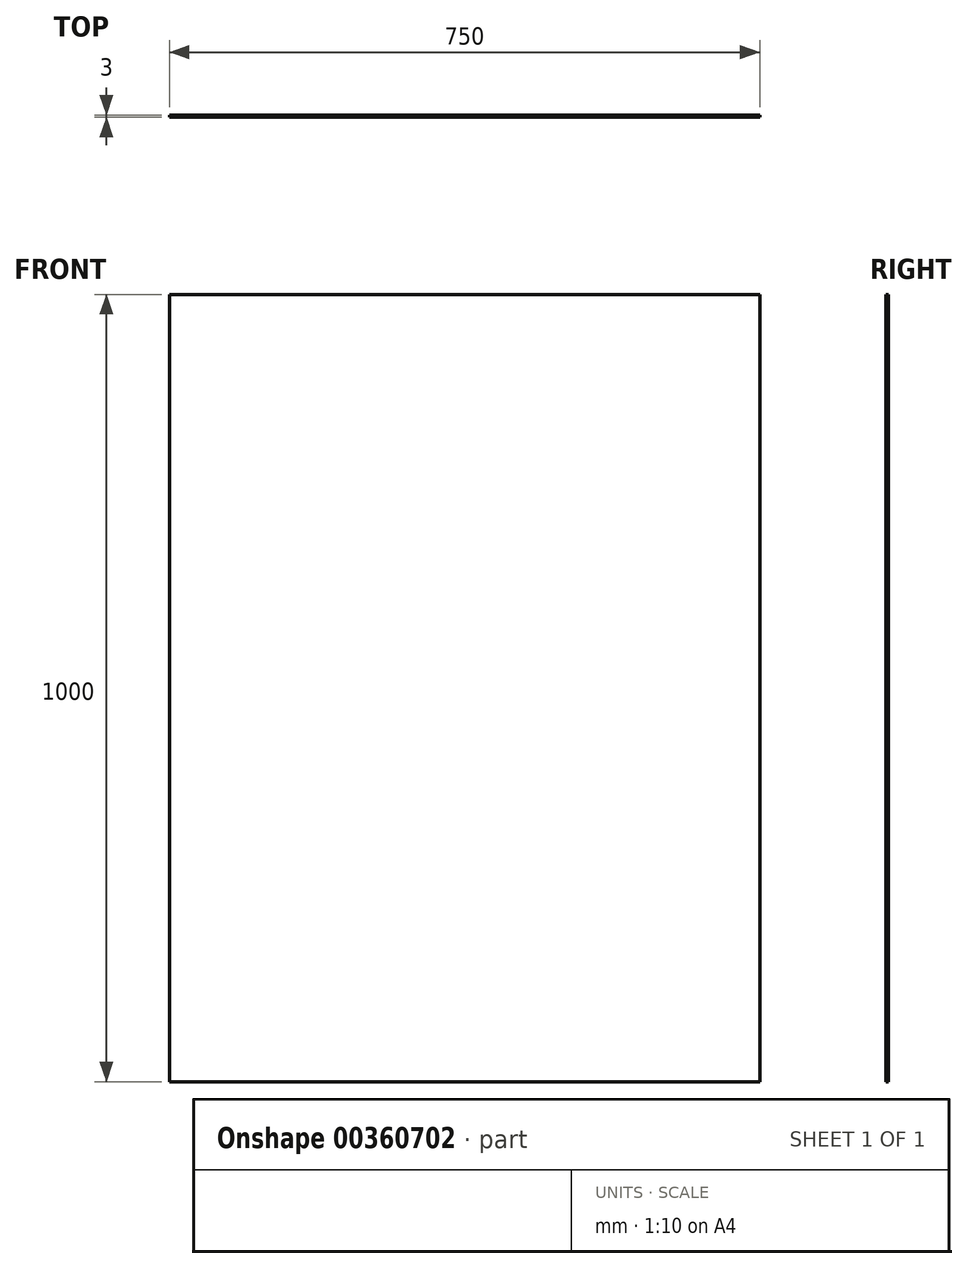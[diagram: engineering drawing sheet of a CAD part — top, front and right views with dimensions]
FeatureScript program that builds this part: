
annotation { "Feature Type Name" : "Feature", "Feature Type Description" : "" }
export const myFeature = defineFeature(function(context is Context, id is Id, definition is map)
    precondition{}
    {
        {
            var Q0;
            Q0=qCreatedBy(makeId("Front.planeOp"),FACE);
            var sketch = newSketch(context, id + "F0", { "sketchPlane" : qUnion([Q0])});
            skLineSegment(sketch, "E0.bottom", {"start": v(0, 0) * mm, "end": v(750, 0) * mm});
            skLineSegment(sketch, "E0.top", {"start": v(0, 1000) * mm, "end": v(750, 1000) * mm});
            skLineSegment(sketch, "E0.left", {"start": v(0, 0) * mm, "end": v(0, 1000) * mm});
            skLineSegment(sketch, "E0.right", {"start": v(750, 0) * mm, "end": v(750, 1000) * mm});
            skSolve(sketch);
        }
        {
            var Q0;
            Q0=makeQuery(id+"F0.imprint","IMPRINT",FACE,{"disambiguationData":[TD([[makeQuery(id+"F0.imprint","IMPRINT",EDGE,{"derivedFrom":sQuery(id+"F0.wireOp",EDGE,"E0.bottom")}),1.0]])]});
            extrude(context, id + "F1", {"entities" : qUnion([Q0]), "depth" : 3 * mm});
        }
    });
